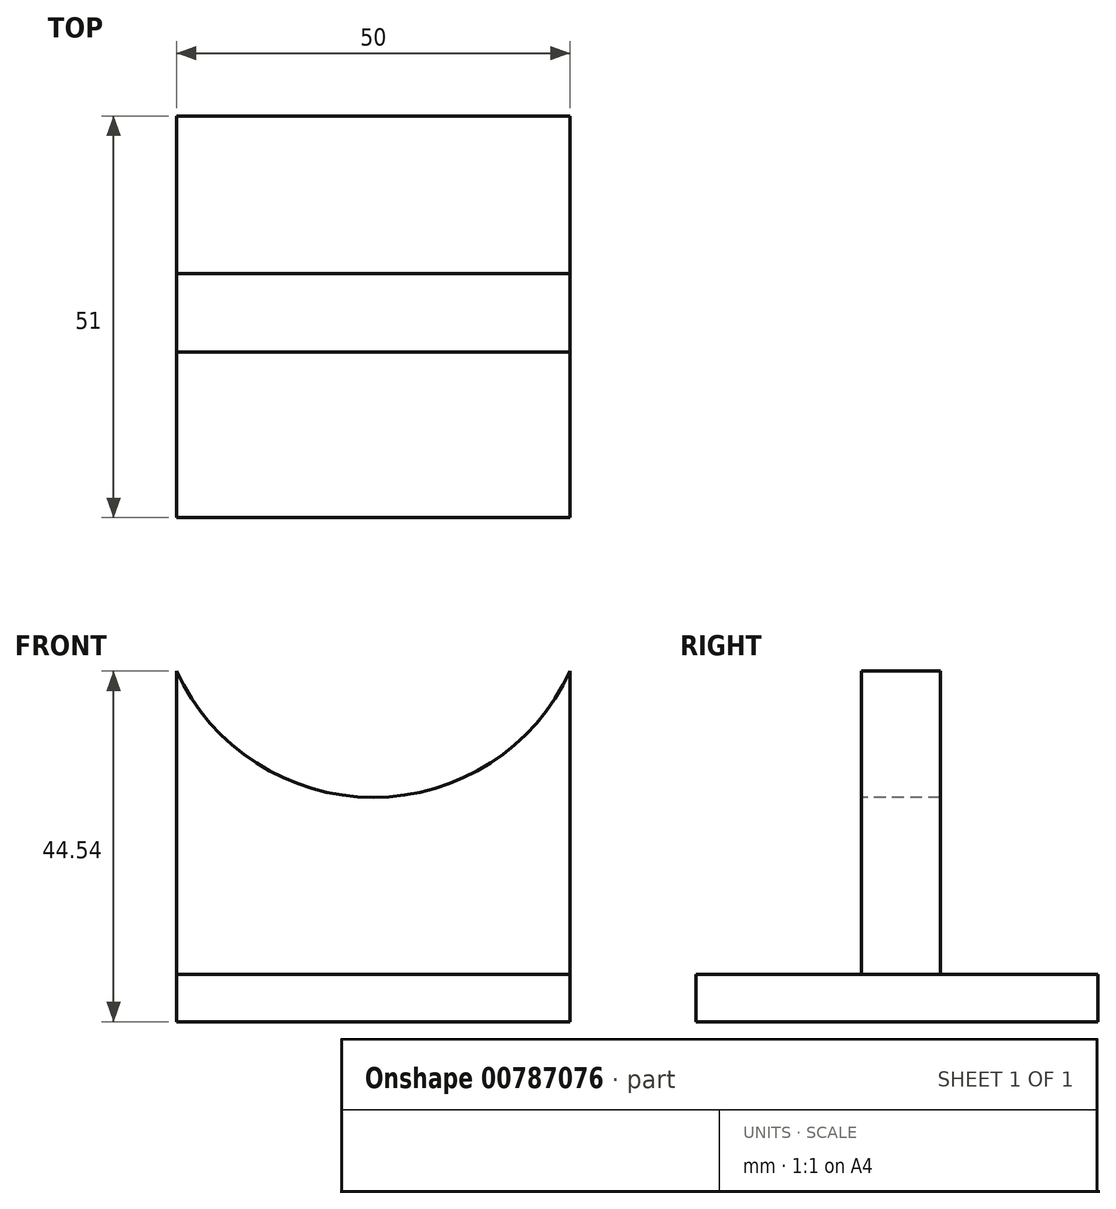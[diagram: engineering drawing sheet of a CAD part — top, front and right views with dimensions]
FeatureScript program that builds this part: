
annotation { "Feature Type Name" : "Feature", "Feature Type Description" : "" }
export const myFeature = defineFeature(function(context is Context, id is Id, definition is map)
    precondition{}
    {
        {
            var Q0;
            Q0=qCreatedBy(makeId("Top.planeOp"),FACE);
            var sketch = newSketch(context, id + "F0", { "sketchPlane" : qUnion([Q0])});
            skLineSegment(sketch, "E0.bottom", {"start": v(-25, 25) * mm, "end": v(25, 25) * mm});
            skLineSegment(sketch, "E0.top", {"start": v(-25, -26) * mm, "end": v(25, -26) * mm});
            skLineSegment(sketch, "E0.left", {"start": v(-25, 25) * mm, "end": v(-25, -26) * mm});
            skLineSegment(sketch, "E0.right", {"start": v(25, 25) * mm, "end": v(25, -26) * mm});
            skSolve(sketch);
        }
        {
            var Q0;
            Q0 = qSketchRegion(id + "F0", true);
            extrude(context, id + "F1", {"entities" : qUnion([Q0]), "depth" : 6 * mm, "offsetDistance" : 25 * mm});
        }
        {
            var Q0;
            Q0=makeQuery(id+"F1.opExtrude","CAP_FACE",FACE,{"disambiguationData":[OSD([sQuery(id+"F0.wireOp",EDGE,"E0.bottom"),sQuery(id+"F0.wireOp",EDGE,"E0.top"),sQuery(id+"F0.wireOp",EDGE,"E0.left"),sQuery(id+"F0.wireOp",EDGE,"E0.right")])],"isStart":false});
            var sketch = newSketch(context, id + "F2", { "sketchPlane" : qUnion([Q0])});
            skLineSegment(sketch, "E1.bottom", {"start": v(-25, 5) * mm, "end": v(25, 5) * mm});
            skLineSegment(sketch, "E1.top", {"start": v(-25, -5) * mm, "end": v(25, -5) * mm});
            skLineSegment(sketch, "E1.left", {"start": v(-25, 5) * mm, "end": v(-25, -5) * mm});
            skLineSegment(sketch, "E1.right", {"start": v(25, 5) * mm, "end": v(25, -5) * mm});
            skSolve(sketch);
        }
        {
            var Q0;
            Q0 = qSketchRegion(id + "F2", true);
            extrude(context, id + "F3", {"entities" : qUnion([Q0]), "depth" : 50 * mm, "offsetDistance" : 25 * mm});
        }
        {
            var Q0;
            Q0=makeQuery(id+"F3.opExtrude","SWEPT_FACE",FACE,{"disambiguationData":[OSD([sQuery(id+"F2.wireOp",EDGE,"E1.top")])]});
            var sketch = newSketch(context, id + "F4", { "sketchPlane" : qUnion([Q0])});
            skCircle(sketch, "E2", {"center": v(0, 56) * mm, "radius": 27.5 * mm});
            skSolve(sketch);
        }
        {
            var Q0;
            Q0=sQuery(id+"F4.wireOp",VERTEX,"E2.center");
            var Q1;
            Q1=makeQuery(id+"F3.opExtrude","SWEPT_BODY",BODY,{"disambiguationData":[OSD([sQuery(id+"F2.wireOp",EDGE,"E1.bottom"),sQuery(id+"F2.wireOp",EDGE,"E1.top"),sQuery(id+"F2.wireOp",EDGE,"E1.left"),sQuery(id+"F2.wireOp",EDGE,"E1.right")])]});
            hole(context, id + "F5", {"style" : HoleStyle.SIMPLE, "endStyle" : HoleEndStyle.THROUGH, "holeDiameter" : 55 * mm, "majorDiameter" : 5 * mm, "isTappedThrough" : true, "tappedDepth" : 12 * mm, "tapClearance" : 3, "startFromSketch" : true, "locations" : qUnion([Q0]), "scope" : qUnion([Q1])});
        }
    });
